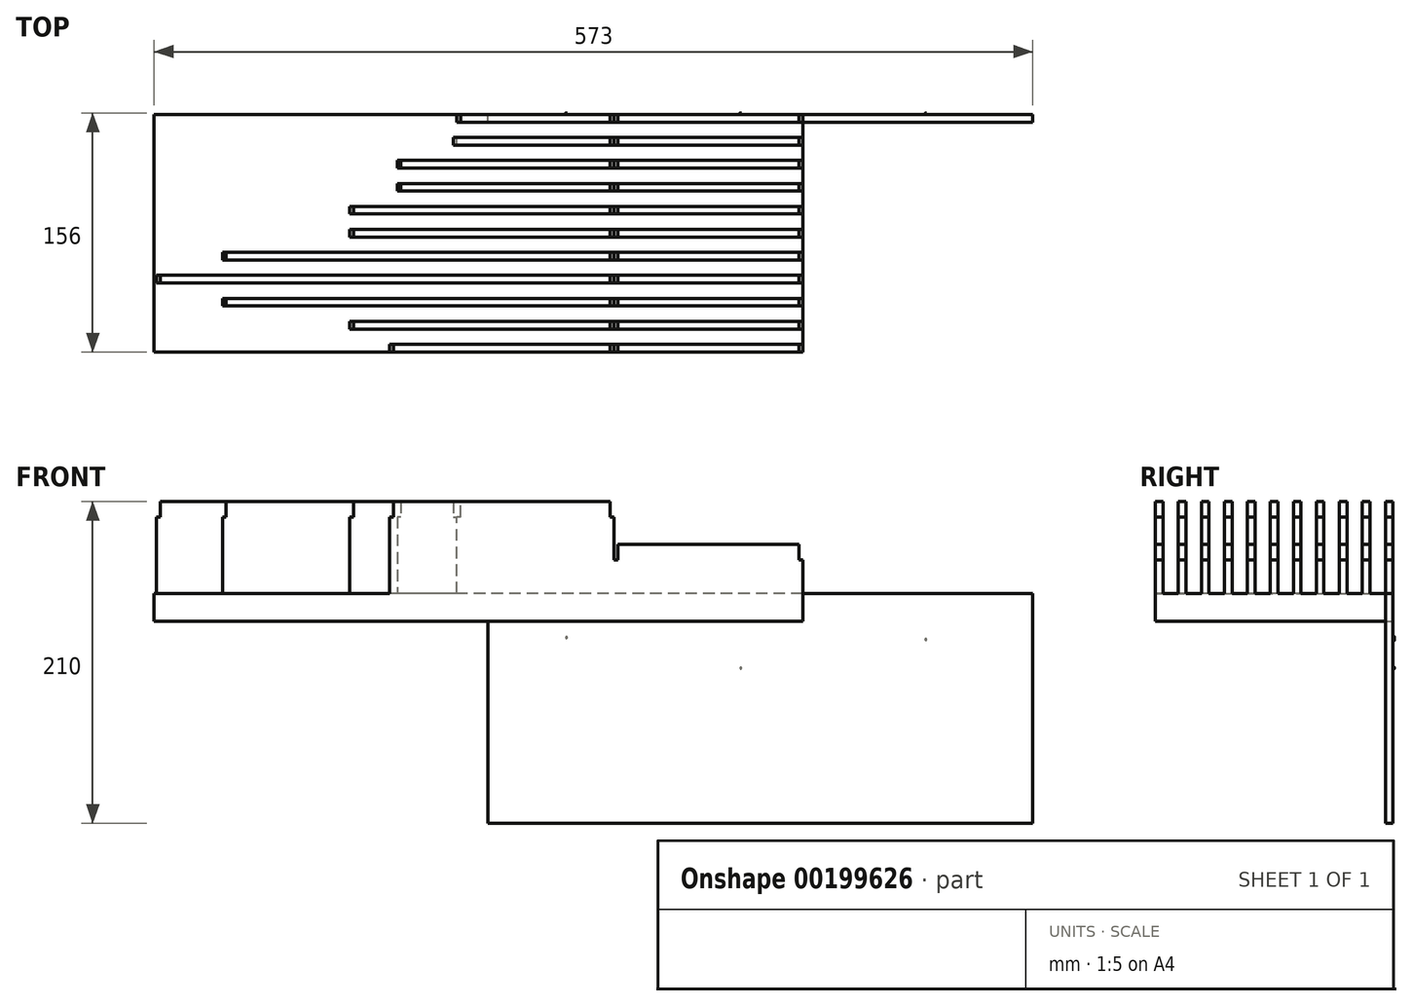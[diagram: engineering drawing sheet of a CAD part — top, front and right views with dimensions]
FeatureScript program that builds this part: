
annotation { "Feature Type Name" : "Feature", "Feature Type Description" : "" }
export const myFeature = defineFeature(function(context is Context, id is Id, definition is map)
    precondition{}
    {
        {
            var Q0;
            Q0=qCreatedBy(makeId("Right.planeOp"),FACE);
            var sketch = newSketch(context, id + "F0", { "sketchPlane" : qUnion([Q0])});
            skLineSegment(sketch, "E0", {"start": v(174.28, 60) * mm, "end": v(179.28, 60) * mm});
            skLineSegment(sketch, "E1", {"start": v(179.28, 60) * mm, "end": v(179.28, 0) * mm});
            skLineSegment(sketch, "E2", {"start": v(179.28, 0) * mm, "end": v(189.28, 0) * mm});
            skLineSegment(sketch, "E3", {"start": v(189.28, 0) * mm, "end": v(189.28, 60) * mm});
            skLineSegment(sketch, "E4", {"start": v(189.28, 60) * mm, "end": v(194.28, 60) * mm});
            skLineSegment(sketch, "E5", {"start": v(194.28, 60) * mm, "end": v(194.28, 0) * mm});
            skLineSegment(sketch, "E6", {"start": v(194.28, 0) * mm, "end": v(204.28, 0) * mm});
            skLineSegment(sketch, "E7", {"start": v(204.28, 0) * mm, "end": v(204.28, 60) * mm});
            skLineSegment(sketch, "E8", {"start": v(204.28, 60) * mm, "end": v(209.28, 60) * mm});
            skLineSegment(sketch, "E9", {"start": v(209.28, 60) * mm, "end": v(209.28, 0) * mm});
            skLineSegment(sketch, "E10", {"start": v(209.28, 0) * mm, "end": v(219.28, 0) * mm});
            skLineSegment(sketch, "E11", {"start": v(219.28, 0) * mm, "end": v(219.28, 60) * mm});
            skLineSegment(sketch, "E12", {"start": v(219.28, 60) * mm, "end": v(224.28, 60) * mm});
            skLineSegment(sketch, "E13", {"start": v(224.28, 60) * mm, "end": v(224.28, 0) * mm});
            skLineSegment(sketch, "E14", {"start": v(224.28, 0) * mm, "end": v(234.28, 0) * mm});
            skLineSegment(sketch, "E15", {"start": v(234.28, 0) * mm, "end": v(234.28, 60) * mm});
            skLineSegment(sketch, "E16", {"start": v(234.28, 60) * mm, "end": v(239.28, 60) * mm});
            skLineSegment(sketch, "E17", {"start": v(239.28, 60) * mm, "end": v(239.28, 0) * mm});
            skLineSegment(sketch, "E18", {"start": v(239.28, 0) * mm, "end": v(249.28, 0) * mm});
            skLineSegment(sketch, "E19", {"start": v(249.28, 0) * mm, "end": v(249.28, 60) * mm});
            skLineSegment(sketch, "E20", {"start": v(249.28, 60) * mm, "end": v(254.28, 60) * mm});
            skLineSegment(sketch, "E21", {"start": v(254.28, 60) * mm, "end": v(254.28, 0) * mm});
            skLineSegment(sketch, "E22", {"start": v(254.28, 0) * mm, "end": v(264.28, 0) * mm});
            skLineSegment(sketch, "E23", {"start": v(264.28, 0) * mm, "end": v(264.28, 60) * mm});
            skLineSegment(sketch, "E24", {"start": v(264.28, 60) * mm, "end": v(269.28, 60) * mm});
            skLineSegment(sketch, "E25", {"start": v(269.28, 60) * mm, "end": v(269.28, 0) * mm});
            skLineSegment(sketch, "E26", {"start": v(269.28, 0) * mm, "end": v(279.28, 0) * mm});
            skLineSegment(sketch, "E27", {"start": v(279.28, 0) * mm, "end": v(279.28, 60) * mm});
            skLineSegment(sketch, "E28", {"start": v(279.28, 60) * mm, "end": v(284.28, 60) * mm});
            skLineSegment(sketch, "E29", {"start": v(284.28, 60) * mm, "end": v(284.28, 0) * mm});
            skLineSegment(sketch, "E30", {"start": v(284.28, 0) * mm, "end": v(294.28, 0) * mm});
            skLineSegment(sketch, "E31", {"start": v(294.28, 0) * mm, "end": v(294.28, 60) * mm});
            skLineSegment(sketch, "E32", {"start": v(294.28, 60) * mm, "end": v(299.28, 60) * mm});
            skLineSegment(sketch, "E33", {"start": v(299.28, 60) * mm, "end": v(299.28, 0) * mm});
            skLineSegment(sketch, "E34", {"start": v(299.28, 0) * mm, "end": v(309.28, 0) * mm});
            skLineSegment(sketch, "E35", {"start": v(309.28, 0) * mm, "end": v(309.28, 60) * mm});
            skLineSegment(sketch, "E36", {"start": v(309.28, 60) * mm, "end": v(314.28, 60) * mm});
            skLineSegment(sketch, "E37", {"start": v(314.28, 60) * mm, "end": v(314.28, 0) * mm});
            skLineSegment(sketch, "E38", {"start": v(314.28, 0) * mm, "end": v(324.28, 0) * mm});
            skLineSegment(sketch, "E39", {"start": v(324.28, 0) * mm, "end": v(324.28, 60) * mm});
            skLineSegment(sketch, "E40", {"start": v(324.28, 60) * mm, "end": v(329.28, 60) * mm});
            skLineSegment(sketch, "E41", {"start": v(329.28, 60) * mm, "end": v(329.28, 60) * mm});
            skLineSegment(sketch, "E42", {"start": v(324.28, -18.06) * mm, "end": v(174.24, -18.06) * mm});
            skLineSegment(sketch, "E43", {"start": v(329.28, 60) * mm, "end": v(329.28, -150) * mm});
            skLineSegment(sketch, "E44", {"start": v(329.28, -150) * mm, "end": v(324.28, -150) * mm});
            skLineSegment(sketch, "E45", {"start": v(324.28, -150) * mm, "end": v(324.28, -18.06) * mm});
            skLineSegment(sketch, "E46", {"start": v(174.28, 60) * mm, "end": v(174.28, -18.06) * mm});
            skSolve(sketch);
        }
        {
            var Q0;
            Q0=makeQuery(id+"F0.imprint","IMPRINT",FACE,{"disambiguationData":[TD([[makeQuery(id+"F0.imprint","IMPRINT",EDGE,{"derivedFrom":sQuery(id+"F0.wireOp",EDGE,"RiP20wC8-9t7q-gec1-XB14-b4tMjAQ6knOq")}),-1.0]])]});
            var Q1;
            Q1=makeQuery(id+"F0.imprint","IMPRINT",FACE,{"disambiguationData":[TD([[makeQuery(id+"F0.imprint","IMPRINT",EDGE,{"derivedFrom":sQuery(id+"F0.wireOp",EDGE,"E0")}),-1.0]])]});
            extrude(context, id + "F1", {"entities" : qUnion([Q0, Q1]), "depth" : 123 * mm});
        }
        {
            var Q0;
            Q0=qSketchRegion(id+"F0",true);
            extrude(context, id + "F2", {"entities" : qUnion([Q0]), "operationType" : NewBodyOperationType.ADD, "oppositeDirection" : true, "depth" : 300 * mm});
        }
        {
            var Q0;
            Q0=makeQuery(id+"F1.opExtrude","SWEPT_FACE",FACE,{"disambiguationData":[OSD([sQuery(id+"F0.wireOp",EDGE,"E43")])]});
            var sketch = newSketch(context, id + "F3", { "sketchPlane" : qUnion([Q0])});
            skCircle(sketch, "E47", {"center": v(-203.34, -30) * mm, "radius": 0.5 * mm});
            skCircle(sketch, "E48", {"center": v(-82.54, -48.6) * mm, "radius": 0.5 * mm});
            skCircle(sketch, "E49", {"center": v(31.1, -28.7) * mm, "radius": 0.5 * mm});
            skSolve(sketch);
        }
        {
            var Q0;
            Q0=qSketchRegion(id+"F3",true);
            extrude(context, id + "F4", {"entities" : qUnion([Q0]), "operationType" : NewBodyOperationType.ADD, "depth" : 1 * mm});
        }
        {
            var Q0;
            Q0=makeQuery(id+"F1.opExtrude","SWEPT_FACE",FACE,{"disambiguationData":[OSD([sQuery(id+"F0.wireOp",EDGE,"E43")])]});
            var sketch = newSketch(context, id + "F5", { "sketchPlane" : qUnion([Q0])});
            skLineSegment(sketch, "E50.bottom", {"start": v(-123, 60) * mm, "end": v(0, 60) * mm});
            skLineSegment(sketch, "E50.top", {"start": v(-123, 32) * mm, "end": v(0, 32) * mm});
            skLineSegment(sketch, "E50.left", {"start": v(-123, 60) * mm, "end": v(-123, 32) * mm});
            skLineSegment(sketch, "E50.right", {"start": v(0, 60) * mm, "end": v(0, 32) * mm});
            skSolve(sketch);
        }
        {
            var Q0;
            Q0=qSketchRegion(id+"F5",true);
            extrude(context, id + "F6", {"entities" : qUnion([Q0]), "operationType" : NewBodyOperationType.REMOVE, "oppositeDirection" : true, "depth" : 300 * mm});
        }
        {
            var Q0;
            Q0=makeQuery(id+"F1.opExtrude","SWEPT_FACE",FACE,{"disambiguationData":[OSD([sQuery(id+"F0.wireOp",EDGE,"E43")])]});
            var sketch = newSketch(context, id + "F7", { "sketchPlane" : qUnion([Q0])});
            skLineSegment(sketch, "E51.bottom", {"start": v(0, 32) * mm, "end": v(-2.5, 32) * mm});
            skLineSegment(sketch, "E51.top", {"start": v(0, 22) * mm, "end": v(-2.5, 22) * mm});
            skLineSegment(sketch, "E51.left", {"start": v(0, 32) * mm, "end": v(0, 22) * mm});
            skLineSegment(sketch, "E51.right", {"start": v(-2.5, 32) * mm, "end": v(-2.5, 22) * mm});
            skLineSegment(sketch, "E52.bottom", {"start": v(0, 60) * mm, "end": v(2.5, 60) * mm});
            skLineSegment(sketch, "E52.top", {"start": v(0, 50) * mm, "end": v(2.5, 50) * mm});
            skLineSegment(sketch, "E52.left", {"start": v(0, 60) * mm, "end": v(0, 50) * mm});
            skLineSegment(sketch, "E52.right", {"start": v(2.5, 60) * mm, "end": v(2.5, 50) * mm});
            skLineSegment(sketch, "E53.bottom", {"start": v(-123, 32) * mm, "end": v(-120.5, 32) * mm});
            skLineSegment(sketch, "E53.top", {"start": v(-123, 22) * mm, "end": v(-120.5, 22) * mm});
            skLineSegment(sketch, "E53.left", {"start": v(-123, 32) * mm, "end": v(-123, 22) * mm});
            skLineSegment(sketch, "E53.right", {"start": v(-120.5, 32) * mm, "end": v(-120.5, 22) * mm});
            skSolve(sketch);
        }
        {
            var Q0;
            Q0=makeQuery(id+"F7.imprint","IMPRINT",FACE,{"disambiguationData":[TD([[makeQuery(id+"F7.imprint","IMPRINT",EDGE,{"derivedFrom":sQuery(id+"F7.wireOp",EDGE,"E51.bottom")}),-1.0]])]});
            var Q1;
            Q1=makeQuery(id+"F7.imprint","IMPRINT",FACE,{"disambiguationData":[TD([[makeQuery(id+"F7.imprint","IMPRINT",EDGE,{"derivedFrom":sQuery(id+"F7.wireOp",EDGE,"E52.bottom")}),-1.0]])]});
            var Q2;
            Q2=makeQuery(id+"F7.imprint","IMPRINT",FACE,{"disambiguationData":[TD([[makeQuery(id+"F7.imprint","IMPRINT",EDGE,{"derivedFrom":sQuery(id+"F7.wireOp",EDGE,"E53.bottom")}),-1.0]])]});
            extrude(context, id + "F8", {"entities" : qUnion([Q0, Q1, Q2]), "operationType" : NewBodyOperationType.REMOVE, "oppositeDirection" : true, "depth" : 300 * mm});
        }
        {
            var Q0;
            Q0=makeQuery(id+"F1.opExtrude","SWEPT_FACE",FACE,{"disambiguationData":[OSD([sQuery(id+"F0.wireOp",EDGE,"E43")])]});
            var sketch = newSketch(context, id + "F9", { "sketchPlane" : qUnion([Q0])});
            skLineSegment(sketch, "E54.bottom", {"start": v(-123, -150) * mm, "end": v(-273, -150) * mm});
            skLineSegment(sketch, "E54.top", {"start": v(-123, 0) * mm, "end": v(-273, 0) * mm});
            skLineSegment(sketch, "E54.left", {"start": v(-123, -150) * mm, "end": v(-123, 0) * mm});
            skLineSegment(sketch, "E54.right", {"start": v(-273, -150) * mm, "end": v(-273, 0) * mm});
            skSolve(sketch);
        }
        {
            var Q0;
            Q0=qSketchRegion(id+"F9",true);
            extrude(context, id + "F10", {"entities" : qUnion([Q0]), "operationType" : NewBodyOperationType.ADD, "oppositeDirection" : true, "depth" : 5 * mm});
        }
        {
            var Q0;
            Q0=makeQuery(id+"F2.opExtrude","CAP_FACE",FACE,{"disambiguationData":[OSD([sQuery(id+"F0.wireOp",EDGE,"E0"),sQuery(id+"F0.wireOp",EDGE,"E1"),sQuery(id+"F0.wireOp",EDGE,"E2"),sQuery(id+"F0.wireOp",EDGE,"E3"),sQuery(id+"F0.wireOp",EDGE,"E4"),sQuery(id+"F0.wireOp",EDGE,"E5"),sQuery(id+"F0.wireOp",EDGE,"E6"),sQuery(id+"F0.wireOp",EDGE,"E7"),sQuery(id+"F0.wireOp",EDGE,"E8"),sQuery(id+"F0.wireOp",EDGE,"E9"),sQuery(id+"F0.wireOp",EDGE,"E10"),sQuery(id+"F0.wireOp",EDGE,"E11"),sQuery(id+"F0.wireOp",EDGE,"E12"),sQuery(id+"F0.wireOp",EDGE,"E13"),sQuery(id+"F0.wireOp",EDGE,"E14"),sQuery(id+"F0.wireOp",EDGE,"E15"),sQuery(id+"F0.wireOp",EDGE,"E16"),sQuery(id+"F0.wireOp",EDGE,"E17"),sQuery(id+"F0.wireOp",EDGE,"E18"),sQuery(id+"F0.wireOp",EDGE,"E19"),sQuery(id+"F0.wireOp",EDGE,"E20"),sQuery(id+"F0.wireOp",EDGE,"E21"),sQuery(id+"F0.wireOp",EDGE,"E22"),sQuery(id+"F0.wireOp",EDGE,"E23"),sQuery(id+"F0.wireOp",EDGE,"E24"),sQuery(id+"F0.wireOp",EDGE,"E25"),sQuery(id+"F0.wireOp",EDGE,"E26"),sQuery(id+"F0.wireOp",EDGE,"E27"),sQuery(id+"F0.wireOp",EDGE,"E28"),sQuery(id+"F0.wireOp",EDGE,"E29"),sQuery(id+"F0.wireOp",EDGE,"E30"),sQuery(id+"F0.wireOp",EDGE,"E31"),sQuery(id+"F0.wireOp",EDGE,"E32"),sQuery(id+"F0.wireOp",EDGE,"E33"),sQuery(id+"F0.wireOp",EDGE,"E34"),sQuery(id+"F0.wireOp",EDGE,"E35"),sQuery(id+"F0.wireOp",EDGE,"E36"),sQuery(id+"F0.wireOp",EDGE,"E37"),sQuery(id+"F0.wireOp",EDGE,"E38"),sQuery(id+"F0.wireOp",EDGE,"E39"),sQuery(id+"F0.wireOp",EDGE,"E40"),sQuery(id+"F0.wireOp",EDGE,"E42"),sQuery(id+"F0.wireOp",EDGE,"E43"),sQuery(id+"F0.wireOp",EDGE,"E44"),sQuery(id+"F0.wireOp",EDGE,"E45"),sQuery(id+"F0.wireOp",EDGE,"E46")])],"isStart":false});
            var sketch = newSketch(context, id + "F11", { "sketchPlane" : qUnion([Q0])});
            skLineSegment(sketch, "E55.bottom", {"start": v(-309.28, 0) * mm, "end": v(-329.28, 0) * mm});
            skLineSegment(sketch, "E55.top", {"start": v(-309.28, 60) * mm, "end": v(-329.28, 60) * mm});
            skLineSegment(sketch, "E55.left", {"start": v(-309.28, 0) * mm, "end": v(-309.28, 60) * mm});
            skLineSegment(sketch, "E55.right", {"start": v(-329.28, 0) * mm, "end": v(-329.28, 60) * mm});
            skSolve(sketch);
        }
        {
            var Q0;
            {var subQ2=sQuery(id+"F11.wireOp",EDGE,"E55.right");Q0=makeQuery(id+"F11.imprint","IMPRINT",FACE,{"disambiguationData":[TD([[makeQuery(id+"F11.imprint","IMPRINT",EDGE,{"derivedFrom":subQ2}),1.0]])]});}
            var Q1;
            {var subQ0=sQuery(id+"F11.wireOp",EDGE,"E55.left");Q1=makeQuery(id+"F11.imprint","IMPRINT",FACE,{"disambiguationData":[TD([[makeQuery(id+"F11.imprint","IMPRINT",EDGE,{"derivedFrom":subQ0}),1.0]])]});}
            extrude(context, id + "F12", {"entities" : qUnion([Q0, Q1]), "operationType" : NewBodyOperationType.REMOVE, "oppositeDirection" : true, "depth" : 197.5 * mm});
        }
        {
            var Q0;
            Q0=makeQuery(id+"F2.opExtrude","CAP_FACE",FACE,{"disambiguationData":[OSD([sQuery(id+"F0.wireOp",EDGE,"E0"),sQuery(id+"F0.wireOp",EDGE,"E1"),sQuery(id+"F0.wireOp",EDGE,"E2"),sQuery(id+"F0.wireOp",EDGE,"E3"),sQuery(id+"F0.wireOp",EDGE,"E4"),sQuery(id+"F0.wireOp",EDGE,"E5"),sQuery(id+"F0.wireOp",EDGE,"E6"),sQuery(id+"F0.wireOp",EDGE,"E7"),sQuery(id+"F0.wireOp",EDGE,"E8"),sQuery(id+"F0.wireOp",EDGE,"E9"),sQuery(id+"F0.wireOp",EDGE,"E10"),sQuery(id+"F0.wireOp",EDGE,"E11"),sQuery(id+"F0.wireOp",EDGE,"E12"),sQuery(id+"F0.wireOp",EDGE,"E13"),sQuery(id+"F0.wireOp",EDGE,"E14"),sQuery(id+"F0.wireOp",EDGE,"E15"),sQuery(id+"F0.wireOp",EDGE,"E16"),sQuery(id+"F0.wireOp",EDGE,"E17"),sQuery(id+"F0.wireOp",EDGE,"E18"),sQuery(id+"F0.wireOp",EDGE,"E19"),sQuery(id+"F0.wireOp",EDGE,"E20"),sQuery(id+"F0.wireOp",EDGE,"E21"),sQuery(id+"F0.wireOp",EDGE,"E22"),sQuery(id+"F0.wireOp",EDGE,"E23"),sQuery(id+"F0.wireOp",EDGE,"E24"),sQuery(id+"F0.wireOp",EDGE,"E25"),sQuery(id+"F0.wireOp",EDGE,"E26"),sQuery(id+"F0.wireOp",EDGE,"E27"),sQuery(id+"F0.wireOp",EDGE,"E28"),sQuery(id+"F0.wireOp",EDGE,"E29"),sQuery(id+"F0.wireOp",EDGE,"E30"),sQuery(id+"F0.wireOp",EDGE,"E31"),sQuery(id+"F0.wireOp",EDGE,"E32"),sQuery(id+"F0.wireOp",EDGE,"E33"),sQuery(id+"F0.wireOp",EDGE,"E34"),sQuery(id+"F0.wireOp",EDGE,"E35"),sQuery(id+"F0.wireOp",EDGE,"E36"),sQuery(id+"F0.wireOp",EDGE,"E37"),sQuery(id+"F0.wireOp",EDGE,"E38"),sQuery(id+"F0.wireOp",EDGE,"E39"),sQuery(id+"F0.wireOp",EDGE,"E40"),sQuery(id+"F0.wireOp",EDGE,"E42"),sQuery(id+"F0.wireOp",EDGE,"E43"),sQuery(id+"F0.wireOp",EDGE,"E44"),sQuery(id+"F0.wireOp",EDGE,"E45"),sQuery(id+"F0.wireOp",EDGE,"E46")])],"isStart":false});
            var sketch = newSketch(context, id + "F13", { "sketchPlane" : qUnion([Q0])});
            skLineSegment(sketch, "E56.bottom", {"start": v(-279.28, 0) * mm, "end": v(-299.28, 0) * mm});
            skLineSegment(sketch, "E56.top", {"start": v(-279.28, 60) * mm, "end": v(-299.28, 60) * mm});
            skLineSegment(sketch, "E56.left", {"start": v(-279.28, 0) * mm, "end": v(-279.28, 60) * mm});
            skLineSegment(sketch, "E56.right", {"start": v(-299.28, 0) * mm, "end": v(-299.28, 60) * mm});
            skSolve(sketch);
        }
        {
            var Q0;
            Q0=qSketchRegion(id+"F13",true);
            extrude(context, id + "F14", {"entities" : qUnion([Q0]), "operationType" : NewBodyOperationType.REMOVE, "oppositeDirection" : true, "depth" : 158.5 * mm});
        }
        {
            var Q0;
            Q0=makeQuery(id+"F2.opExtrude","CAP_FACE",FACE,{"disambiguationData":[OSD([sQuery(id+"F0.wireOp",EDGE,"E0"),sQuery(id+"F0.wireOp",EDGE,"E1"),sQuery(id+"F0.wireOp",EDGE,"E2"),sQuery(id+"F0.wireOp",EDGE,"E3"),sQuery(id+"F0.wireOp",EDGE,"E4"),sQuery(id+"F0.wireOp",EDGE,"E5"),sQuery(id+"F0.wireOp",EDGE,"E6"),sQuery(id+"F0.wireOp",EDGE,"E7"),sQuery(id+"F0.wireOp",EDGE,"E8"),sQuery(id+"F0.wireOp",EDGE,"E9"),sQuery(id+"F0.wireOp",EDGE,"E10"),sQuery(id+"F0.wireOp",EDGE,"E11"),sQuery(id+"F0.wireOp",EDGE,"E12"),sQuery(id+"F0.wireOp",EDGE,"E13"),sQuery(id+"F0.wireOp",EDGE,"E14"),sQuery(id+"F0.wireOp",EDGE,"E15"),sQuery(id+"F0.wireOp",EDGE,"E16"),sQuery(id+"F0.wireOp",EDGE,"E17"),sQuery(id+"F0.wireOp",EDGE,"E18"),sQuery(id+"F0.wireOp",EDGE,"E19"),sQuery(id+"F0.wireOp",EDGE,"E20"),sQuery(id+"F0.wireOp",EDGE,"E21"),sQuery(id+"F0.wireOp",EDGE,"E22"),sQuery(id+"F0.wireOp",EDGE,"E23"),sQuery(id+"F0.wireOp",EDGE,"E24"),sQuery(id+"F0.wireOp",EDGE,"E25"),sQuery(id+"F0.wireOp",EDGE,"E26"),sQuery(id+"F0.wireOp",EDGE,"E27"),sQuery(id+"F0.wireOp",EDGE,"E28"),sQuery(id+"F0.wireOp",EDGE,"E29"),sQuery(id+"F0.wireOp",EDGE,"E30"),sQuery(id+"F0.wireOp",EDGE,"E31"),sQuery(id+"F0.wireOp",EDGE,"E32"),sQuery(id+"F0.wireOp",EDGE,"E33"),sQuery(id+"F0.wireOp",EDGE,"E34"),sQuery(id+"F0.wireOp",EDGE,"E35"),sQuery(id+"F0.wireOp",EDGE,"E36"),sQuery(id+"F0.wireOp",EDGE,"E37"),sQuery(id+"F0.wireOp",EDGE,"E38"),sQuery(id+"F0.wireOp",EDGE,"E39"),sQuery(id+"F0.wireOp",EDGE,"E40"),sQuery(id+"F0.wireOp",EDGE,"E42"),sQuery(id+"F0.wireOp",EDGE,"E43"),sQuery(id+"F0.wireOp",EDGE,"E44"),sQuery(id+"F0.wireOp",EDGE,"E45"),sQuery(id+"F0.wireOp",EDGE,"E46")])],"isStart":false});
            var sketch = newSketch(context, id + "F15", { "sketchPlane" : qUnion([Q0])});
            skLineSegment(sketch, "E57.bottom", {"start": v(-269.28, 60) * mm, "end": v(-249.28, 60) * mm});
            skLineSegment(sketch, "E57.top", {"start": v(-269.28, 0) * mm, "end": v(-249.28, 0) * mm});
            skLineSegment(sketch, "E57.left", {"start": v(-269.28, 60) * mm, "end": v(-269.28, 0) * mm});
            skLineSegment(sketch, "E57.right", {"start": v(-249.28, 60) * mm, "end": v(-249.28, 0) * mm});
            skLineSegment(sketch, "E58.bottom", {"start": v(-194.28, 0) * mm, "end": v(-189.28, 0) * mm});
            skLineSegment(sketch, "E58.top", {"start": v(-194.28, 60) * mm, "end": v(-189.28, 60) * mm});
            skLineSegment(sketch, "E58.left", {"start": v(-194.28, 0) * mm, "end": v(-194.28, 60) * mm});
            skLineSegment(sketch, "E58.right", {"start": v(-189.28, 0) * mm, "end": v(-189.28, 60) * mm});
            skSolve(sketch);
        }
        {
            var Q0;
            Q0=qSketchRegion(id+"F15",true);
            extrude(context, id + "F16", {"entities" : qUnion([Q0]), "operationType" : NewBodyOperationType.REMOVE, "oppositeDirection" : true, "depth" : 127.5 * mm});
        }
        {
            var Q0;
            Q0=makeQuery(id+"F2.opExtrude","CAP_FACE",FACE,{"disambiguationData":[OSD([sQuery(id+"F0.wireOp",EDGE,"E0"),sQuery(id+"F0.wireOp",EDGE,"E1"),sQuery(id+"F0.wireOp",EDGE,"E2"),sQuery(id+"F0.wireOp",EDGE,"E3"),sQuery(id+"F0.wireOp",EDGE,"E4"),sQuery(id+"F0.wireOp",EDGE,"E5"),sQuery(id+"F0.wireOp",EDGE,"E6"),sQuery(id+"F0.wireOp",EDGE,"E7"),sQuery(id+"F0.wireOp",EDGE,"E8"),sQuery(id+"F0.wireOp",EDGE,"E9"),sQuery(id+"F0.wireOp",EDGE,"E10"),sQuery(id+"F0.wireOp",EDGE,"E11"),sQuery(id+"F0.wireOp",EDGE,"E12"),sQuery(id+"F0.wireOp",EDGE,"E13"),sQuery(id+"F0.wireOp",EDGE,"E14"),sQuery(id+"F0.wireOp",EDGE,"E15"),sQuery(id+"F0.wireOp",EDGE,"E16"),sQuery(id+"F0.wireOp",EDGE,"E17"),sQuery(id+"F0.wireOp",EDGE,"E18"),sQuery(id+"F0.wireOp",EDGE,"E19"),sQuery(id+"F0.wireOp",EDGE,"E20"),sQuery(id+"F0.wireOp",EDGE,"E21"),sQuery(id+"F0.wireOp",EDGE,"E22"),sQuery(id+"F0.wireOp",EDGE,"E23"),sQuery(id+"F0.wireOp",EDGE,"E24"),sQuery(id+"F0.wireOp",EDGE,"E25"),sQuery(id+"F0.wireOp",EDGE,"E26"),sQuery(id+"F0.wireOp",EDGE,"E27"),sQuery(id+"F0.wireOp",EDGE,"E28"),sQuery(id+"F0.wireOp",EDGE,"E29"),sQuery(id+"F0.wireOp",EDGE,"E30"),sQuery(id+"F0.wireOp",EDGE,"E31"),sQuery(id+"F0.wireOp",EDGE,"E32"),sQuery(id+"F0.wireOp",EDGE,"E33"),sQuery(id+"F0.wireOp",EDGE,"E34"),sQuery(id+"F0.wireOp",EDGE,"E35"),sQuery(id+"F0.wireOp",EDGE,"E36"),sQuery(id+"F0.wireOp",EDGE,"E37"),sQuery(id+"F0.wireOp",EDGE,"E38"),sQuery(id+"F0.wireOp",EDGE,"E39"),sQuery(id+"F0.wireOp",EDGE,"E40"),sQuery(id+"F0.wireOp",EDGE,"E42"),sQuery(id+"F0.wireOp",EDGE,"E43"),sQuery(id+"F0.wireOp",EDGE,"E44"),sQuery(id+"F0.wireOp",EDGE,"E45"),sQuery(id+"F0.wireOp",EDGE,"E46")])],"isStart":false});
            var sketch = newSketch(context, id + "F17", { "sketchPlane" : qUnion([Q0])});
            skLineSegment(sketch, "E59.bottom", {"start": v(-239.28, 60) * mm, "end": v(-234.28, 60) * mm});
            skLineSegment(sketch, "E59.top", {"start": v(-239.28, 0) * mm, "end": v(-234.28, 0) * mm});
            skLineSegment(sketch, "E59.left", {"start": v(-239.28, 60) * mm, "end": v(-239.28, 0) * mm});
            skLineSegment(sketch, "E59.right", {"start": v(-234.28, 60) * mm, "end": v(-234.28, 0) * mm});
            skLineSegment(sketch, "E60.bottom", {"start": v(-209.28, 60) * mm, "end": v(-204.28, 60) * mm});
            skLineSegment(sketch, "E60.top", {"start": v(-209.28, 0) * mm, "end": v(-204.28, 0) * mm});
            skLineSegment(sketch, "E60.left", {"start": v(-209.28, 60) * mm, "end": v(-209.28, 0) * mm});
            skLineSegment(sketch, "E60.right", {"start": v(-204.28, 60) * mm, "end": v(-204.28, 0) * mm});
            skSolve(sketch);
        }
        {
            var Q0;
            Q0=qSketchRegion(id+"F17",true);
            extrude(context, id + "F18", {"entities" : qUnion([Q0]), "operationType" : NewBodyOperationType.REMOVE, "oppositeDirection" : true, "depth" : 44.5 * mm});
        }
        {
            var Q0;
            Q0=makeQuery(id+"F2.opExtrude","CAP_FACE",FACE,{"disambiguationData":[OSD([sQuery(id+"F0.wireOp",EDGE,"E0"),sQuery(id+"F0.wireOp",EDGE,"E1"),sQuery(id+"F0.wireOp",EDGE,"E2"),sQuery(id+"F0.wireOp",EDGE,"E3"),sQuery(id+"F0.wireOp",EDGE,"E4"),sQuery(id+"F0.wireOp",EDGE,"E5"),sQuery(id+"F0.wireOp",EDGE,"E6"),sQuery(id+"F0.wireOp",EDGE,"E7"),sQuery(id+"F0.wireOp",EDGE,"E8"),sQuery(id+"F0.wireOp",EDGE,"E9"),sQuery(id+"F0.wireOp",EDGE,"E10"),sQuery(id+"F0.wireOp",EDGE,"E11"),sQuery(id+"F0.wireOp",EDGE,"E12"),sQuery(id+"F0.wireOp",EDGE,"E13"),sQuery(id+"F0.wireOp",EDGE,"E14"),sQuery(id+"F0.wireOp",EDGE,"E15"),sQuery(id+"F0.wireOp",EDGE,"E16"),sQuery(id+"F0.wireOp",EDGE,"E17"),sQuery(id+"F0.wireOp",EDGE,"E18"),sQuery(id+"F0.wireOp",EDGE,"E19"),sQuery(id+"F0.wireOp",EDGE,"E20"),sQuery(id+"F0.wireOp",EDGE,"E21"),sQuery(id+"F0.wireOp",EDGE,"E22"),sQuery(id+"F0.wireOp",EDGE,"E23"),sQuery(id+"F0.wireOp",EDGE,"E24"),sQuery(id+"F0.wireOp",EDGE,"E25"),sQuery(id+"F0.wireOp",EDGE,"E26"),sQuery(id+"F0.wireOp",EDGE,"E27"),sQuery(id+"F0.wireOp",EDGE,"E28"),sQuery(id+"F0.wireOp",EDGE,"E29"),sQuery(id+"F0.wireOp",EDGE,"E30"),sQuery(id+"F0.wireOp",EDGE,"E31"),sQuery(id+"F0.wireOp",EDGE,"E32"),sQuery(id+"F0.wireOp",EDGE,"E33"),sQuery(id+"F0.wireOp",EDGE,"E34"),sQuery(id+"F0.wireOp",EDGE,"E35"),sQuery(id+"F0.wireOp",EDGE,"E36"),sQuery(id+"F0.wireOp",EDGE,"E37"),sQuery(id+"F0.wireOp",EDGE,"E38"),sQuery(id+"F0.wireOp",EDGE,"E39"),sQuery(id+"F0.wireOp",EDGE,"E40"),sQuery(id+"F0.wireOp",EDGE,"E42"),sQuery(id+"F0.wireOp",EDGE,"E43"),sQuery(id+"F0.wireOp",EDGE,"E44"),sQuery(id+"F0.wireOp",EDGE,"E45"),sQuery(id+"F0.wireOp",EDGE,"E46")])],"isStart":false});
            var sketch = newSketch(context, id + "F19", { "sketchPlane" : qUnion([Q0])});
            skLineSegment(sketch, "E61.bottom", {"start": v(-219.28, 0) * mm, "end": v(-224.28, 0) * mm});
            skLineSegment(sketch, "E61.top", {"start": v(-219.28, 60) * mm, "end": v(-224.28, 60) * mm});
            skLineSegment(sketch, "E61.left", {"start": v(-219.28, 0) * mm, "end": v(-219.28, 60) * mm});
            skLineSegment(sketch, "E61.right", {"start": v(-224.28, 0) * mm, "end": v(-224.28, 60) * mm});
            skSolve(sketch);
        }
        {
            var Q0;
            Q0=qSketchRegion(id+"F19",true);
            extrude(context, id + "F20", {"entities" : qUnion([Q0]), "operationType" : NewBodyOperationType.REMOVE, "oppositeDirection" : true, "depth" : 1.5 * mm});
        }
        {
            var Q0;
            Q0=makeQuery(id+"F2.opExtrude","CAP_FACE",FACE,{"disambiguationData":[OSD([sQuery(id+"F0.wireOp",EDGE,"E0"),sQuery(id+"F0.wireOp",EDGE,"E1"),sQuery(id+"F0.wireOp",EDGE,"E2"),sQuery(id+"F0.wireOp",EDGE,"E3"),sQuery(id+"F0.wireOp",EDGE,"E4"),sQuery(id+"F0.wireOp",EDGE,"E5"),sQuery(id+"F0.wireOp",EDGE,"E6"),sQuery(id+"F0.wireOp",EDGE,"E7"),sQuery(id+"F0.wireOp",EDGE,"E8"),sQuery(id+"F0.wireOp",EDGE,"E9"),sQuery(id+"F0.wireOp",EDGE,"E10"),sQuery(id+"F0.wireOp",EDGE,"E11"),sQuery(id+"F0.wireOp",EDGE,"E12"),sQuery(id+"F0.wireOp",EDGE,"E13"),sQuery(id+"F0.wireOp",EDGE,"E14"),sQuery(id+"F0.wireOp",EDGE,"E15"),sQuery(id+"F0.wireOp",EDGE,"E16"),sQuery(id+"F0.wireOp",EDGE,"E17"),sQuery(id+"F0.wireOp",EDGE,"E18"),sQuery(id+"F0.wireOp",EDGE,"E19"),sQuery(id+"F0.wireOp",EDGE,"E20"),sQuery(id+"F0.wireOp",EDGE,"E21"),sQuery(id+"F0.wireOp",EDGE,"E22"),sQuery(id+"F0.wireOp",EDGE,"E23"),sQuery(id+"F0.wireOp",EDGE,"E24"),sQuery(id+"F0.wireOp",EDGE,"E25"),sQuery(id+"F0.wireOp",EDGE,"E26"),sQuery(id+"F0.wireOp",EDGE,"E27"),sQuery(id+"F0.wireOp",EDGE,"E28"),sQuery(id+"F0.wireOp",EDGE,"E29"),sQuery(id+"F0.wireOp",EDGE,"E30"),sQuery(id+"F0.wireOp",EDGE,"E31"),sQuery(id+"F0.wireOp",EDGE,"E32"),sQuery(id+"F0.wireOp",EDGE,"E33"),sQuery(id+"F0.wireOp",EDGE,"E34"),sQuery(id+"F0.wireOp",EDGE,"E35"),sQuery(id+"F0.wireOp",EDGE,"E36"),sQuery(id+"F0.wireOp",EDGE,"E37"),sQuery(id+"F0.wireOp",EDGE,"E38"),sQuery(id+"F0.wireOp",EDGE,"E39"),sQuery(id+"F0.wireOp",EDGE,"E40"),sQuery(id+"F0.wireOp",EDGE,"E42"),sQuery(id+"F0.wireOp",EDGE,"E43"),sQuery(id+"F0.wireOp",EDGE,"E44"),sQuery(id+"F0.wireOp",EDGE,"E45"),sQuery(id+"F0.wireOp",EDGE,"E46")])],"isStart":false});
            var sketch = newSketch(context, id + "F21", { "sketchPlane" : qUnion([Q0])});
            skLineSegment(sketch, "E62.bottom", {"start": v(-179.28, 0) * mm, "end": v(-174.28, 0) * mm});
            skLineSegment(sketch, "E62.top", {"start": v(-179.28, 60) * mm, "end": v(-174.28, 60) * mm});
            skLineSegment(sketch, "E62.left", {"start": v(-179.28, 0) * mm, "end": v(-179.28, 60) * mm});
            skLineSegment(sketch, "E62.right", {"start": v(-174.28, 0) * mm, "end": v(-174.28, 60) * mm});
            skSolve(sketch);
        }
        {
            var Q0;
            Q0=qSketchRegion(id+"F21",true);
            extrude(context, id + "F22", {"entities" : qUnion([Q0]), "operationType" : NewBodyOperationType.REMOVE, "oppositeDirection" : true, "depth" : 153.5 * mm});
        }
        {
            var Q0;
            Q0=makeQuery(id+"F20.boolean.opBoolean","COPY",FACE,{"derivedFrom":makeQuery(id+"F20.opExtrude","CAP_FACE",FACE,{"disambiguationData":[OSD([sQuery(id+"F19.wireOp",EDGE,"E61.bottom"),sQuery(id+"F19.wireOp",EDGE,"E61.top"),sQuery(id+"F19.wireOp",EDGE,"E61.left"),sQuery(id+"F19.wireOp",EDGE,"E61.right")])],"isStart":false})});
            var sketch = newSketch(context, id + "F23", { "sketchPlane" : qUnion([Q0])});
            skLineSegment(sketch, "E63.bottom", {"start": v(-224.28, 60) * mm, "end": v(-219.28, 60) * mm});
            skLineSegment(sketch, "E63.top", {"start": v(-224.28, 50) * mm, "end": v(-219.28, 50) * mm});
            skLineSegment(sketch, "E63.left", {"start": v(-224.28, 60) * mm, "end": v(-224.28, 50) * mm});
            skLineSegment(sketch, "E63.right", {"start": v(-219.28, 60) * mm, "end": v(-219.28, 50) * mm});
            skSolve(sketch);
        }
        {
            var Q0;
            Q0=qSketchRegion(id+"F23",true);
            extrude(context, id + "F24", {"entities" : qUnion([Q0]), "operationType" : NewBodyOperationType.REMOVE, "oppositeDirection" : true, "depth" : 2.5 * mm});
        }
        {
            var Q0;
            Q0=makeQuery(id+"F18.boolean.opBoolean","COPY",FACE,{"derivedFrom":makeQuery(id+"F18.opExtrude","CAP_FACE",FACE,{"disambiguationData":[OSD([sQuery(id+"F17.wireOp",EDGE,"E59.bottom"),sQuery(id+"F17.wireOp",EDGE,"E59.top"),sQuery(id+"F17.wireOp",EDGE,"E59.left"),sQuery(id+"F17.wireOp",EDGE,"E59.right")])],"isStart":false})});
            var sketch = newSketch(context, id + "F25", { "sketchPlane" : qUnion([Q0])});
            skLineSegment(sketch, "E64.bottom", {"start": v(-239.28, 60) * mm, "end": v(-234.28, 60) * mm});
            skLineSegment(sketch, "E64.top", {"start": v(-239.28, 50) * mm, "end": v(-234.28, 50) * mm});
            skLineSegment(sketch, "E64.left", {"start": v(-239.28, 60) * mm, "end": v(-239.28, 50) * mm});
            skLineSegment(sketch, "E64.right", {"start": v(-234.28, 60) * mm, "end": v(-234.28, 50) * mm});
            skSolve(sketch);
        }
        {
            var Q0;
            Q0=qSketchRegion(id+"F25",true);
            extrude(context, id + "F26", {"entities" : qUnion([Q0]), "operationType" : NewBodyOperationType.REMOVE, "oppositeDirection" : true, "depth" : 2.5 * mm});
        }
        {
            var Q0;
            Q0=makeQuery(id+"F18.boolean.opBoolean","COPY",FACE,{"derivedFrom":makeQuery(id+"F18.opExtrude","CAP_FACE",FACE,{"disambiguationData":[OSD([sQuery(id+"F17.wireOp",EDGE,"E60.bottom"),sQuery(id+"F17.wireOp",EDGE,"E60.top"),sQuery(id+"F17.wireOp",EDGE,"E60.left"),sQuery(id+"F17.wireOp",EDGE,"E60.right")])],"isStart":false})});
            var sketch = newSketch(context, id + "F27", { "sketchPlane" : qUnion([Q0])});
            skLineSegment(sketch, "E65.bottom", {"start": v(-209.28, 60) * mm, "end": v(-204.28, 60) * mm});
            skLineSegment(sketch, "E65.top", {"start": v(-209.28, 50) * mm, "end": v(-204.28, 50) * mm});
            skLineSegment(sketch, "E65.left", {"start": v(-209.28, 60) * mm, "end": v(-209.28, 50) * mm});
            skLineSegment(sketch, "E65.right", {"start": v(-204.28, 60) * mm, "end": v(-204.28, 50) * mm});
            skSolve(sketch);
        }
        {
            var Q0;
            Q0=qSketchRegion(id+"F27",true);
            extrude(context, id + "F28", {"entities" : qUnion([Q0]), "operationType" : NewBodyOperationType.REMOVE, "oppositeDirection" : true, "depth" : 2.5 * mm});
        }
        {
            var Q0;
            {var subQ7=sQuery(id+"F0.wireOp",EDGE,"E19");var subQ10=sQuery(id+"F15.wireOp",EDGE,"E57.top");Q0=makeQuery(id+"F16.boolean.opBoolean","COPY",FACE,{"disambiguationData":[TD([makeQuery(id+"F1.opExtrude","SWEPT_FACE",FACE,{"disambiguationData":[OSD([subQ7])]})])],"derivedFrom":makeQuery(id+"F16.opExtrude","CAP_FACE",FACE,{"disambiguationData":[OSD([sQuery(id+"F15.wireOp",EDGE,"E57.bottom"),subQ10,sQuery(id+"F15.wireOp",EDGE,"E57.left"),sQuery(id+"F15.wireOp",EDGE,"E57.right")])],"isStart":false})});}
            var sketch = newSketch(context, id + "F29", { "sketchPlane" : qUnion([Q0])});
            skLineSegment(sketch, "E66.bottom", {"start": v(-254.28, 60) * mm, "end": v(-249.28, 60) * mm});
            skLineSegment(sketch, "E66.top", {"start": v(-254.28, 50) * mm, "end": v(-249.28, 50) * mm});
            skLineSegment(sketch, "E66.left", {"start": v(-254.28, 60) * mm, "end": v(-254.28, 50) * mm});
            skLineSegment(sketch, "E66.right", {"start": v(-249.28, 60) * mm, "end": v(-249.28, 50) * mm});
            skSolve(sketch);
        }
        {
            var Q0;
            Q0=qSketchRegion(id+"F29",true);
            extrude(context, id + "F30", {"entities" : qUnion([Q0]), "operationType" : NewBodyOperationType.REMOVE, "oppositeDirection" : true, "depth" : 2.5 * mm});
        }
        {
            var Q0;
            Q0=makeQuery(id+"F16.boolean.opBoolean","COPY",FACE,{"derivedFrom":makeQuery(id+"F16.opExtrude","CAP_FACE",FACE,{"disambiguationData":[OSD([sQuery(id+"F15.wireOp",EDGE,"E58.bottom"),sQuery(id+"F15.wireOp",EDGE,"E58.top"),sQuery(id+"F15.wireOp",EDGE,"E58.left"),sQuery(id+"F15.wireOp",EDGE,"E58.right")])],"isStart":false})});
            var sketch = newSketch(context, id + "F31", { "sketchPlane" : qUnion([Q0])});
            skLineSegment(sketch, "E67.bottom", {"start": v(-194.28, 60) * mm, "end": v(-189.28, 60) * mm});
            skLineSegment(sketch, "E67.top", {"start": v(-194.28, 50) * mm, "end": v(-189.28, 50) * mm});
            skLineSegment(sketch, "E67.left", {"start": v(-194.28, 60) * mm, "end": v(-194.28, 50) * mm});
            skLineSegment(sketch, "E67.right", {"start": v(-189.28, 60) * mm, "end": v(-189.28, 50) * mm});
            skSolve(sketch);
        }
        {
            var Q0;
            Q0=qSketchRegion(id+"F31",true);
            extrude(context, id + "F32", {"entities" : qUnion([Q0]), "operationType" : NewBodyOperationType.REMOVE, "oppositeDirection" : true, "depth" : 2.5 * mm});
        }
        {
            var Q0;
            {var subQ3=sQuery(id+"F0.wireOp",EDGE,"E23");var subQ10=sQuery(id+"F15.wireOp",EDGE,"E57.top");Q0=makeQuery(id+"F16.boolean.opBoolean","COPY",FACE,{"disambiguationData":[TD([makeQuery(id+"F1.opExtrude","SWEPT_FACE",FACE,{"disambiguationData":[OSD([subQ3])]})])],"derivedFrom":makeQuery(id+"F16.opExtrude","CAP_FACE",FACE,{"disambiguationData":[OSD([sQuery(id+"F15.wireOp",EDGE,"E57.bottom"),subQ10,sQuery(id+"F15.wireOp",EDGE,"E57.left"),sQuery(id+"F15.wireOp",EDGE,"E57.right")])],"isStart":false})});}
            var sketch = newSketch(context, id + "F33", { "sketchPlane" : qUnion([Q0])});
            skLineSegment(sketch, "E68.bottom", {"start": v(-269.28, 60) * mm, "end": v(-264.28, 60) * mm});
            skLineSegment(sketch, "E68.top", {"start": v(-269.28, 50) * mm, "end": v(-264.28, 50) * mm});
            skLineSegment(sketch, "E68.left", {"start": v(-269.28, 60) * mm, "end": v(-269.28, 50) * mm});
            skLineSegment(sketch, "E68.right", {"start": v(-264.28, 60) * mm, "end": v(-264.28, 50) * mm});
            skSolve(sketch);
        }
        {
            var Q0;
            Q0=qSketchRegion(id+"F33",true);
            extrude(context, id + "F34", {"entities" : qUnion([Q0]), "operationType" : NewBodyOperationType.REMOVE, "oppositeDirection" : true, "depth" : 2.5 * mm});
        }
        {
            var Q0;
            Q0=makeQuery(id+"F22.boolean.opBoolean","COPY",FACE,{"derivedFrom":makeQuery(id+"F22.opExtrude","CAP_FACE",FACE,{"disambiguationData":[OSD([sQuery(id+"F21.wireOp",EDGE,"E62.bottom"),sQuery(id+"F21.wireOp",EDGE,"E62.top"),sQuery(id+"F21.wireOp",EDGE,"E62.left"),sQuery(id+"F21.wireOp",EDGE,"E62.right")])],"isStart":false})});
            var sketch = newSketch(context, id + "F35", { "sketchPlane" : qUnion([Q0])});
            skLineSegment(sketch, "E69.bottom", {"start": v(-179.28, 60) * mm, "end": v(-174.28, 60) * mm});
            skLineSegment(sketch, "E69.top", {"start": v(-179.28, 50) * mm, "end": v(-174.28, 50) * mm});
            skLineSegment(sketch, "E69.left", {"start": v(-179.28, 60) * mm, "end": v(-179.28, 50) * mm});
            skLineSegment(sketch, "E69.right", {"start": v(-174.28, 60) * mm, "end": v(-174.28, 50) * mm});
            skSolve(sketch);
        }
        {
            var Q0;
            Q0=qSketchRegion(id+"F35",true);
            extrude(context, id + "F36", {"entities" : qUnion([Q0]), "operationType" : NewBodyOperationType.REMOVE, "oppositeDirection" : true, "depth" : 2.5 * mm});
        }
        {
            var Q0;
            {var subQ3=sQuery(id+"F0.wireOp",EDGE,"E27");var subQ7=sQuery(id+"F13.wireOp",EDGE,"E56.bottom");Q0=makeQuery(id+"F14.boolean.opBoolean","COPY",FACE,{"disambiguationData":[TD([makeQuery(id+"F1.opExtrude","SWEPT_FACE",FACE,{"disambiguationData":[OSD([subQ3])]})])],"derivedFrom":makeQuery(id+"F14.opExtrude","CAP_FACE",FACE,{"disambiguationData":[OSD([subQ7,sQuery(id+"F13.wireOp",EDGE,"E56.top"),sQuery(id+"F13.wireOp",EDGE,"E56.left"),sQuery(id+"F13.wireOp",EDGE,"E56.right")])],"isStart":false})});}
            var sketch = newSketch(context, id + "F37", { "sketchPlane" : qUnion([Q0])});
            skLineSegment(sketch, "E70.bottom", {"start": v(-284.28, 60) * mm, "end": v(-279.28, 60) * mm});
            skLineSegment(sketch, "E70.top", {"start": v(-284.28, 50) * mm, "end": v(-279.28, 50) * mm});
            skLineSegment(sketch, "E70.left", {"start": v(-284.28, 60) * mm, "end": v(-284.28, 50) * mm});
            skLineSegment(sketch, "E70.right", {"start": v(-279.28, 60) * mm, "end": v(-279.28, 50) * mm});
            skSolve(sketch);
        }
        {
            var Q0;
            Q0=qSketchRegion(id+"F37",true);
            extrude(context, id + "F38", {"entities" : qUnion([Q0]), "operationType" : NewBodyOperationType.REMOVE, "oppositeDirection" : true, "depth" : 2.5 * mm});
        }
        {
            var Q0;
            {var subQ0=sQuery(id+"F0.wireOp",EDGE,"E31");var subQ7=sQuery(id+"F13.wireOp",EDGE,"E56.bottom");Q0=makeQuery(id+"F14.boolean.opBoolean","COPY",FACE,{"disambiguationData":[TD([makeQuery(id+"F1.opExtrude","SWEPT_FACE",FACE,{"disambiguationData":[OSD([subQ0])]})])],"derivedFrom":makeQuery(id+"F14.opExtrude","CAP_FACE",FACE,{"disambiguationData":[OSD([subQ7,sQuery(id+"F13.wireOp",EDGE,"E56.top"),sQuery(id+"F13.wireOp",EDGE,"E56.left"),sQuery(id+"F13.wireOp",EDGE,"E56.right")])],"isStart":false})});}
            var sketch = newSketch(context, id + "F39", { "sketchPlane" : qUnion([Q0])});
            skLineSegment(sketch, "E71.bottom", {"start": v(-299.28, 60) * mm, "end": v(-294.28, 60) * mm});
            skLineSegment(sketch, "E71.top", {"start": v(-299.28, 50) * mm, "end": v(-294.28, 50) * mm});
            skLineSegment(sketch, "E71.left", {"start": v(-299.28, 60) * mm, "end": v(-299.28, 50) * mm});
            skLineSegment(sketch, "E71.right", {"start": v(-294.28, 60) * mm, "end": v(-294.28, 50) * mm});
            skSolve(sketch);
        }
        {
            var Q0;
            Q0=qSketchRegion(id+"F39",true);
            extrude(context, id + "F40", {"entities" : qUnion([Q0]), "operationType" : NewBodyOperationType.REMOVE, "oppositeDirection" : true, "depth" : 2.5 * mm});
        }
        {
            var Q0;
            Q0=makeQuery(id+"F12.boolean.opBoolean","COPY",FACE,{"derivedFrom":makeQuery(id+"F12.opExtrude","CAP_FACE",FACE,{"disambiguationData":[OSD([sQuery(id+"F0.wireOp",EDGE,"E37"),sQuery(id+"F11.wireOp",EDGE,"E55.bottom"),sQuery(id+"F11.wireOp",EDGE,"E55.top"),sQuery(id+"F11.wireOp",EDGE,"E55.left")])],"isStart":false})});
            var sketch = newSketch(context, id + "F41", { "sketchPlane" : qUnion([Q0])});
            skLineSegment(sketch, "E72.bottom", {"start": v(-314.28, 60) * mm, "end": v(-309.28, 60) * mm});
            skLineSegment(sketch, "E72.top", {"start": v(-314.28, 50) * mm, "end": v(-309.28, 50) * mm});
            skLineSegment(sketch, "E72.left", {"start": v(-314.28, 60) * mm, "end": v(-314.28, 50) * mm});
            skLineSegment(sketch, "E72.right", {"start": v(-309.28, 60) * mm, "end": v(-309.28, 50) * mm});
            skSolve(sketch);
        }
        {
            var Q0;
            Q0=qSketchRegion(id+"F41",true);
            extrude(context, id + "F42", {"entities" : qUnion([Q0]), "operationType" : NewBodyOperationType.ADD, "depth" : 2.5 * mm});
        }
        {
            var Q0;
            Q0=makeQuery(id+"F12.boolean.opBoolean","COPY",FACE,{"derivedFrom":makeQuery(id+"F12.opExtrude","CAP_FACE",FACE,{"disambiguationData":[OSD([sQuery(id+"F0.wireOp",EDGE,"E39"),sQuery(id+"F11.wireOp",EDGE,"E55.bottom"),sQuery(id+"F11.wireOp",EDGE,"E55.top"),sQuery(id+"F11.wireOp",EDGE,"E55.right")])],"isStart":false})});
            var sketch = newSketch(context, id + "F43", { "sketchPlane" : qUnion([Q0])});
            skLineSegment(sketch, "E73.bottom", {"start": v(-329.28, 60) * mm, "end": v(-324.28, 60) * mm});
            skLineSegment(sketch, "E73.top", {"start": v(-329.28, 50) * mm, "end": v(-324.28, 50) * mm});
            skLineSegment(sketch, "E73.left", {"start": v(-329.28, 60) * mm, "end": v(-329.28, 50) * mm});
            skLineSegment(sketch, "E73.right", {"start": v(-324.28, 60) * mm, "end": v(-324.28, 50) * mm});
            skSolve(sketch);
        }
        {
            var Q0;
            Q0=qSketchRegion(id+"F43",true);
            extrude(context, id + "F44", {"entities" : qUnion([Q0]), "operationType" : NewBodyOperationType.REMOVE, "oppositeDirection" : true, "depth" : 2.5 * mm});
        }
        {
            var Q0;
            {var subQ0=sQuery(id+"F0.wireOp",EDGE,"E43");Q0=makeQuery(id+"F10.boolean.opBoolean","MERGE",FACE,{"derivedFrom":[makeQuery(id+"F2.boolean.opBoolean","MERGE",FACE,{"derivedFrom":[makeQuery(id+"F1.opExtrude","SWEPT_FACE",FACE,{"disambiguationData":[OSD([subQ0])]}),makeQuery(id+"F2.opExtrude","SWEPT_FACE",FACE,{"disambiguationData":[OSD([subQ0])]})]}),makeQuery(id+"F10.opExtrude","CAP_FACE",FACE,{"disambiguationData":[OSD([sQuery(id+"F9.wireOp",EDGE,"E54.bottom"),sQuery(id+"F9.wireOp",EDGE,"E54.top"),sQuery(id+"F9.wireOp",EDGE,"E54.left"),sQuery(id+"F9.wireOp",EDGE,"E54.right")])],"isStart":true})]});}
            var sketch = newSketch(context, id + "F45", { "sketchPlane" : qUnion([Q0])});
            skLineSegment(sketch, "E74.bottom", {"start": v(300, -150) * mm, "end": v(82.43, -150) * mm});
            skLineSegment(sketch, "E74.top", {"start": v(300, -18.06) * mm, "end": v(82.43, -18.06) * mm});
            skLineSegment(sketch, "E74.left", {"start": v(300, -150) * mm, "end": v(300, -18.06) * mm});
            skLineSegment(sketch, "E74.right", {"start": v(82.43, -150) * mm, "end": v(82.43, -18.06) * mm});
            skSolve(sketch);
        }
        {
            var Q0;
            Q0=qSketchRegion(id+"F45",true);
            extrude(context, id + "F46", {"entities" : qUnion([Q0]), "operationType" : NewBodyOperationType.REMOVE, "oppositeDirection" : true, "depth" : 5 * mm});
        }
    });
